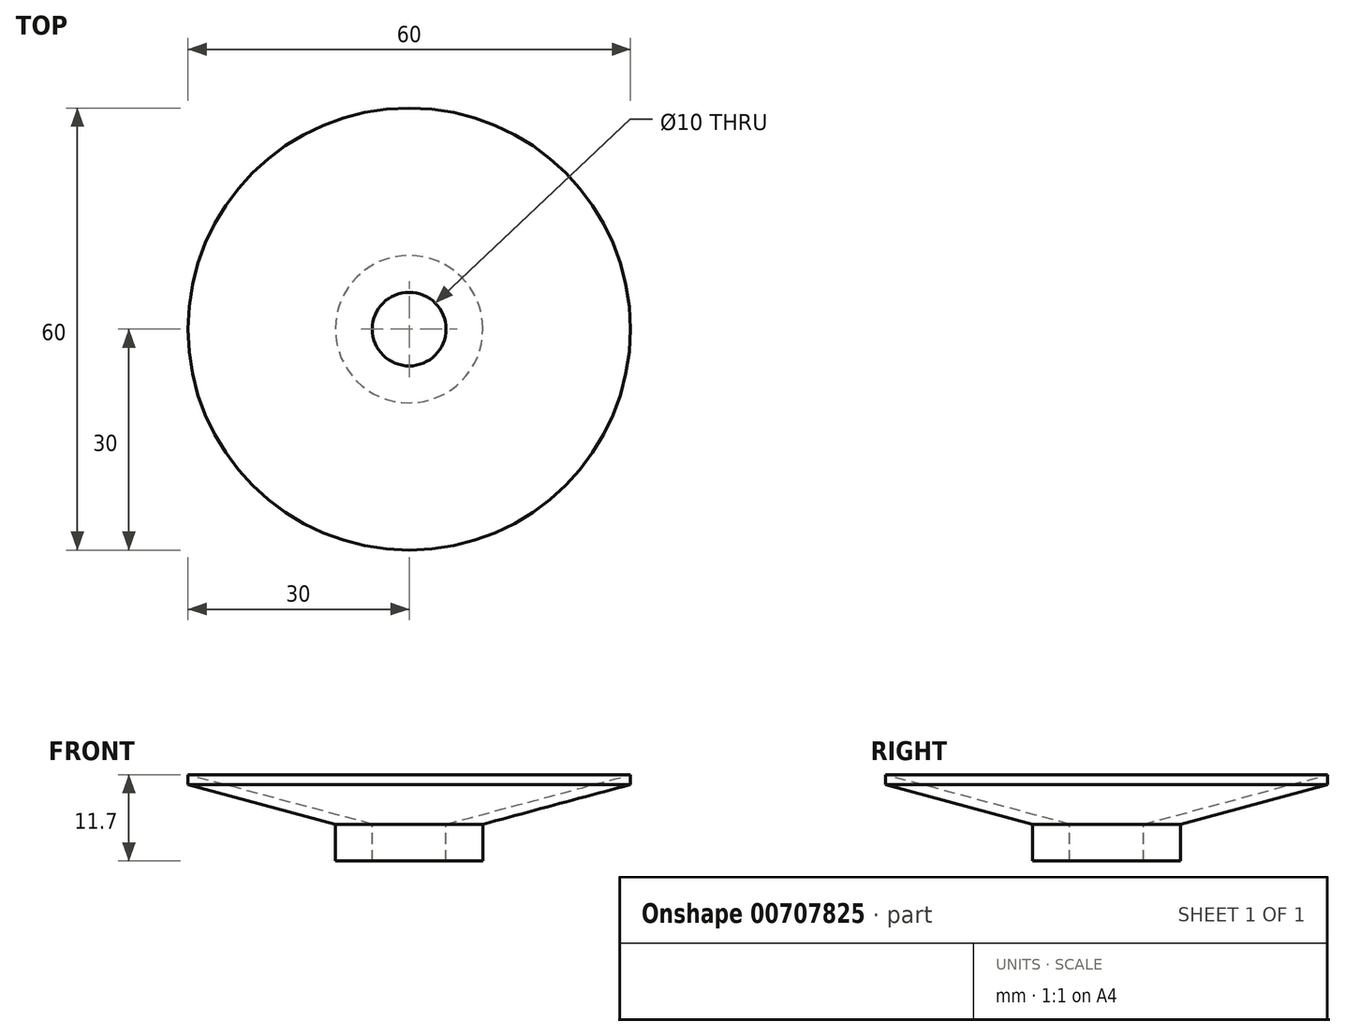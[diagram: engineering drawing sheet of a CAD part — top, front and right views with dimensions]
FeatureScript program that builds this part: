
annotation { "Feature Type Name" : "Feature", "Feature Type Description" : "" }
export const myFeature = defineFeature(function(context is Context, id is Id, definition is map)
    precondition{}
    {
        {
            var Q0;
            Q0=qCreatedBy(makeId("Top.planeOp"),FACE);
            var sketch = newSketch(context, id + "F0", { "sketchPlane" : qUnion([Q0])});
            skCircle(sketch, "E0", {"center": v(0, 0) * mm, "radius": 5 * mm});
            skCircle(sketch, "E1", {"center": v(0, 0) * mm, "radius": 10 * mm});
            skSolve(sketch);
        }
        {
            var Q0;
            Q0=makeQuery(id+"F0.imprint","IMPRINT",FACE,{"disambiguationData":[TD([[makeQuery(id+"F0.imprint","IMPRINT",EDGE,{"derivedFrom":sQuery(id+"F0.wireOp",EDGE,"E0")}),-1.0]])]});
            extrude(context, id + "F1", {"entities" : qUnion([Q0]), "oppositeDirection" : true, "depth" : 5 * mm, "offsetDistance" : 25 * mm});
        }
        {
            var Q0;
            Q0=qCreatedBy(makeId("Front.planeOp"),FACE);
            var sketch = newSketch(context, id + "F2", { "sketchPlane" : qUnion([Q0])});
            skLineSegment(sketch, "E2", {"start": v(-10, 0) * mm, "end": v(-30, 5.36) * mm});
            skLineSegment(sketch, "E3", {"start": v(-30, 5.36) * mm, "end": v(-30, 6.7) * mm});
            skLineSegment(sketch, "E4", {"start": v(-30, 6.7) * mm, "end": v(-5, 0) * mm});
            skLineSegment(sketch, "E5", {"start": v(-10, 0) * mm, "end": v(-5, 0) * mm});
            skSolve(sketch);
        }
        {
            var Q0;
            Q0=qCreatedBy(makeId("Front.planeOp"),FACE);
            var sketch = newSketch(context, id + "F3", { "sketchPlane" : qUnion([Q0])});
            skLineSegment(sketch, "E6", {"start": v(0, 27.9) * mm, "end": v(0, -50.72) * mm});
            skSolve(sketch);
        }
        {
            var Q0;
            Q0 = qSketchRegion(id + "F2", true);
            var Q1;
            Q1=sQuery(id+"F3.wireOp",EDGE,"E6");
            revolve(context, id + "F4", {"operationType" : NewBodyOperationType.ADD, "surfaceOperationType" : NewSurfaceOperationType.NEW, "entities" : qUnion([Q0]), "axis" : qUnion([Q1]), "revolveType" : RevolveType.FULL});
        }
    });
